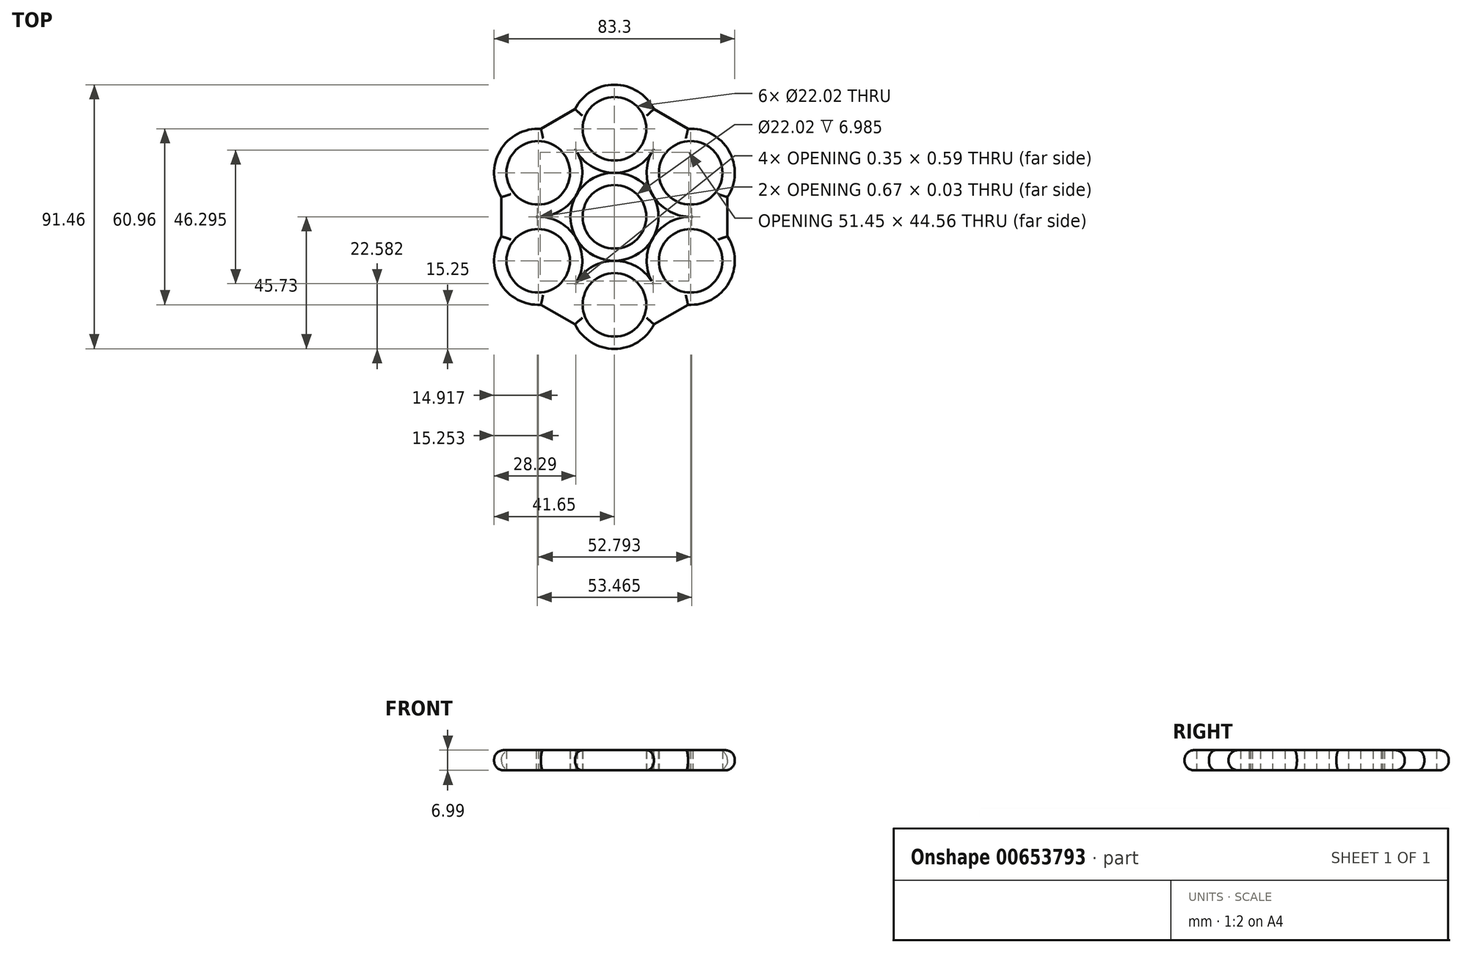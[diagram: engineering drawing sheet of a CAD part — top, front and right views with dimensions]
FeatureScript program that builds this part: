
annotation { "Feature Type Name" : "Feature", "Feature Type Description" : "" }
export const myFeature = defineFeature(function(context is Context, id is Id, definition is map)
    precondition{}
    {
        {
            var Q0;
            Q0=qCreatedBy(makeId("Top.planeOp"),FACE);
            var sketch = newSketch(context, id + "F0", { "sketchPlane" : qUnion([Q0])});
            skCircle(sketch, "E0", {"center": v(0, 0) * mm, "radius": 11.01 * mm});
            skLineSegment(sketch, "E1", {"start": v(0, 0) * mm, "end": v(0, 30.48) * mm});
            skLineSegment(sketch, "E2", {"start": v(0, 0) * mm, "end": v(26.4, -15.24) * mm});
            skLineSegment(sketch, "E3", {"start": v(0, 0) * mm, "end": v(-26.4, -15.24) * mm});
            skLineSegment(sketch, "E4", {"start": v(0, 0) * mm, "end": v(-26.4, 15.24) * mm});
            skLineSegment(sketch, "E5", {"start": v(0, 0) * mm, "end": v(0, -30.48) * mm});
            skLineSegment(sketch, "E6", {"start": v(0, 0) * mm, "end": v(26.4, 15.24) * mm});
            skCircle(sketch, "E7.cCircle", {"center": v(0, 30.48) * mm, "radius": 11.01 * mm, "construction": true});
            skLineSegment(sketch, "E7.0", {"start": v(6.36, 19.47) * mm, "end": v(-6.36, 19.47) * mm});
            skLineSegment(sketch, "E7.1", {"start": v(-6.36, 19.47) * mm, "end": v(-12.71, 30.48) * mm});
            skLineSegment(sketch, "E7.2", {"start": v(-12.71, 30.48) * mm, "end": v(-6.36, 41.5) * mm});
            skLineSegment(sketch, "E7.3", {"start": v(-6.36, 41.5) * mm, "end": v(6.36, 41.5) * mm});
            skLineSegment(sketch, "E7.4", {"start": v(6.36, 41.5) * mm, "end": v(12.71, 30.48) * mm});
            skLineSegment(sketch, "E7.5", {"start": v(12.71, 30.48) * mm, "end": v(6.36, 19.47) * mm});
            skPoint(sketch, "E7.0.midPoint", {"position": v(0, 19.47) * mm});
            skCircle(sketch, "E8.cCircle", {"center": v(26.4, 15.24) * mm, "radius": 11.01 * mm, "construction": true});
            skLineSegment(sketch, "E8.0", {"start": v(20.04, 4.23) * mm, "end": v(13.68, 15.24) * mm});
            skLineSegment(sketch, "E8.1", {"start": v(13.68, 15.24) * mm, "end": v(20.04, 26.25) * mm});
            skLineSegment(sketch, "E8.2", {"start": v(20.04, 26.25) * mm, "end": v(32.75, 26.25) * mm});
            skLineSegment(sketch, "E8.3", {"start": v(32.75, 26.25) * mm, "end": v(39.11, 15.24) * mm});
            skLineSegment(sketch, "E8.4", {"start": v(39.11, 15.24) * mm, "end": v(32.75, 4.23) * mm});
            skLineSegment(sketch, "E8.5", {"start": v(32.75, 4.23) * mm, "end": v(20.04, 4.23) * mm});
            skPoint(sketch, "E8.0.midPoint", {"position": v(16.86, 9.73) * mm});
            skCircle(sketch, "E9.cCircle", {"center": v(26.4, -15.24) * mm, "radius": 11.01 * mm, "construction": true});
            skLineSegment(sketch, "E9.0", {"start": v(13.68, -15.24) * mm, "end": v(20.04, -4.23) * mm});
            skLineSegment(sketch, "E9.1", {"start": v(20.04, -4.23) * mm, "end": v(32.75, -4.23) * mm});
            skLineSegment(sketch, "E9.2", {"start": v(32.75, -4.23) * mm, "end": v(39.11, -15.24) * mm});
            skLineSegment(sketch, "E9.3", {"start": v(39.11, -15.24) * mm, "end": v(32.75, -26.25) * mm});
            skLineSegment(sketch, "E9.4", {"start": v(32.75, -26.25) * mm, "end": v(20.04, -26.25) * mm});
            skLineSegment(sketch, "E9.5", {"start": v(20.04, -26.25) * mm, "end": v(13.68, -15.24) * mm});
            skPoint(sketch, "E9.0.midPoint", {"position": v(16.86, -9.73) * mm});
            skCircle(sketch, "E10.cCircle", {"center": v(0, -30.48) * mm, "radius": 11.01 * mm, "construction": true});
            skLineSegment(sketch, "E10.0", {"start": v(-6.36, -19.47) * mm, "end": v(6.36, -19.47) * mm});
            skLineSegment(sketch, "E10.1", {"start": v(6.36, -19.47) * mm, "end": v(12.71, -30.48) * mm});
            skLineSegment(sketch, "E10.2", {"start": v(12.71, -30.48) * mm, "end": v(6.36, -41.5) * mm});
            skLineSegment(sketch, "E10.3", {"start": v(6.36, -41.5) * mm, "end": v(-6.36, -41.5) * mm});
            skLineSegment(sketch, "E10.4", {"start": v(-6.36, -41.5) * mm, "end": v(-12.71, -30.48) * mm});
            skLineSegment(sketch, "E10.5", {"start": v(-12.71, -30.48) * mm, "end": v(-6.36, -19.47) * mm});
            skPoint(sketch, "E10.0.midPoint", {"position": v(0, -19.47) * mm});
            skCircle(sketch, "E11.cCircle", {"center": v(-26.4, -15.24) * mm, "radius": 11.01 * mm, "construction": true});
            skLineSegment(sketch, "E11.0", {"start": v(-20.04, -4.23) * mm, "end": v(-13.68, -15.24) * mm});
            skLineSegment(sketch, "E11.1", {"start": v(-13.68, -15.24) * mm, "end": v(-20.04, -26.25) * mm});
            skLineSegment(sketch, "E11.2", {"start": v(-20.04, -26.25) * mm, "end": v(-32.75, -26.25) * mm});
            skLineSegment(sketch, "E11.3", {"start": v(-32.75, -26.25) * mm, "end": v(-39.11, -15.24) * mm});
            skLineSegment(sketch, "E11.4", {"start": v(-39.11, -15.24) * mm, "end": v(-32.75, -4.23) * mm});
            skLineSegment(sketch, "E11.5", {"start": v(-32.75, -4.23) * mm, "end": v(-20.04, -4.23) * mm});
            skPoint(sketch, "E11.0.midPoint", {"position": v(-16.86, -9.73) * mm});
            skCircle(sketch, "E12.cCircle", {"center": v(-26.4, 15.24) * mm, "radius": 11.01 * mm, "construction": true});
            skLineSegment(sketch, "E12.0", {"start": v(-13.68, 15.24) * mm, "end": v(-20.04, 4.23) * mm});
            skLineSegment(sketch, "E12.1", {"start": v(-20.04, 4.23) * mm, "end": v(-32.75, 4.23) * mm});
            skLineSegment(sketch, "E12.2", {"start": v(-32.75, 4.23) * mm, "end": v(-39.11, 15.24) * mm});
            skLineSegment(sketch, "E12.3", {"start": v(-39.11, 15.24) * mm, "end": v(-32.75, 26.25) * mm});
            skLineSegment(sketch, "E12.4", {"start": v(-32.75, 26.25) * mm, "end": v(-20.04, 26.25) * mm});
            skLineSegment(sketch, "E12.5", {"start": v(-20.04, 26.25) * mm, "end": v(-13.68, 15.24) * mm});
            skPoint(sketch, "E12.0.midPoint", {"position": v(-16.86, 9.73) * mm});
            skCircle(sketch, "E13", {"center": v(0, 0) * mm, "radius": 15.23 * mm});
            skPoint(sketch, "E14.startSnap0", {"position": v(-16.86, 20.75) * mm});
            skLineSegment(sketch, "E15", {"start": v(-16.86, 20.75) * mm, "end": v(-9.54, 24.97) * mm});
            skLineSegment(sketch, "E16", {"start": v(-26.4, 4.23) * mm, "end": v(-26.4, -4.23) * mm});
            skLineSegment(sketch, "E17", {"start": v(26.4, 4.23) * mm, "end": v(26.4, -4.23) * mm});
            skLineSegment(sketch, "E18", {"start": v(-16.86, -20.75) * mm, "end": v(-9.54, -24.97) * mm});
            skLineSegment(sketch, "E19", {"start": v(16.86, -20.75) * mm, "end": v(9.54, -24.97) * mm});
            skLineSegment(sketch, "E20", {"start": v(16.86, 20.75) * mm, "end": v(9.54, 24.97) * mm});
            skLineSegment(sketch, "E21", {"start": v(-32.75, 26.25) * mm, "end": v(-6.36, 41.5) * mm});
            skLineSegment(sketch, "E22", {"start": v(-39.11, 15.24) * mm, "end": v(-39.11, -15.24) * mm});
            skLineSegment(sketch, "E23", {"start": v(39.11, 15.24) * mm, "end": v(39.11, -15.24) * mm});
            skLineSegment(sketch, "E24", {"start": v(6.36, -41.5) * mm, "end": v(32.75, -26.25) * mm});
            skLineSegment(sketch, "E25", {"start": v(-6.36, -41.5) * mm, "end": v(-32.75, -26.25) * mm});
            skLineSegment(sketch, "E26", {"start": v(6.36, 41.5) * mm, "end": v(32.75, 26.25) * mm});
            skCircle(sketch, "E27", {"center": v(-26.4, 15.24) * mm, "radius": 15.25 * mm});
            skCircle(sketch, "E28", {"center": v(0, 30.48) * mm, "radius": 15.25 * mm});
            skCircle(sketch, "E29", {"center": v(26.4, 15.24) * mm, "radius": 15.25 * mm});
            skCircle(sketch, "E30", {"center": v(26.4, -15.24) * mm, "radius": 15.25 * mm});
            skCircle(sketch, "E31", {"center": v(0, -30.48) * mm, "radius": 15.25 * mm});
            skCircle(sketch, "E32", {"center": v(-26.4, -15.24) * mm, "radius": 15.25 * mm});
            skCircle(sketch, "E33", {"center": v(0, 30.48) * mm, "radius": 11.01 * mm});
            skCircle(sketch, "E34", {"center": v(26.4, 15.24) * mm, "radius": 11.01 * mm});
            skCircle(sketch, "E35", {"center": v(26.4, -15.24) * mm, "radius": 11.01 * mm});
            skCircle(sketch, "E36", {"center": v(0, -30.48) * mm, "radius": 11.01 * mm});
            skCircle(sketch, "E37", {"center": v(-26.4, 15.24) * mm, "radius": 11.01 * mm});
            skCircle(sketch, "E38", {"center": v(-26.4, -15.24) * mm, "radius": 11.01 * mm});
            skSolve(sketch);
        }
        {
            var Q0;
            {var subQ3=sQuery(id+"F0.wireOp",EDGE,"E7.2");Q0=makeQuery(id+"F0.imprint","IMPRINT",FACE,{"disambiguationData":[TD([[makeQuery(id+"F0.imprint","IMPRINT",EDGE,{"derivedFrom":subQ3}),1.0]])]});}
            var Q1;
            {var subQ4=sQuery(id+"F0.wireOp",EDGE,"E7.4");Q1=makeQuery(id+"F0.imprint","IMPRINT",FACE,{"disambiguationData":[TD([[makeQuery(id+"F0.imprint","IMPRINT",EDGE,{"derivedFrom":subQ4}),1.0]])]});}
            var Q2;
            {var subQ4=sQuery(id+"F0.wireOp",EDGE,"E8.4");Q2=makeQuery(id+"F0.imprint","IMPRINT",FACE,{"disambiguationData":[TD([[makeQuery(id+"F0.imprint","IMPRINT",EDGE,{"derivedFrom":subQ4}),1.0]])]});}
            var Q3;
            {var subQ4=sQuery(id+"F0.wireOp",EDGE,"E9.4");Q3=makeQuery(id+"F0.imprint","IMPRINT",FACE,{"disambiguationData":[TD([[makeQuery(id+"F0.imprint","IMPRINT",EDGE,{"derivedFrom":subQ4}),1.0]])]});}
            var Q4;
            {var subQ4=sQuery(id+"F0.wireOp",EDGE,"E10.4");Q4=makeQuery(id+"F0.imprint","IMPRINT",FACE,{"disambiguationData":[TD([[makeQuery(id+"F0.imprint","IMPRINT",EDGE,{"derivedFrom":subQ4}),1.0]])]});}
            var Q5;
            {var subQ4=sQuery(id+"F0.wireOp",EDGE,"E11.4");Q5=makeQuery(id+"F0.imprint","IMPRINT",FACE,{"disambiguationData":[TD([[makeQuery(id+"F0.imprint","IMPRINT",EDGE,{"derivedFrom":subQ4}),1.0]])]});}
            var Q6;
            {var subQ0=sQuery(id+"F0.wireOp",EDGE,"E4");var subQ1=sQuery(id+"F0.wireOp",EDGE,"E0");var subQ2=makeQuery(id+"F0.imprint","INTERSECT",VERTEX,{"derivedFrom":[subQ1,subQ0]});Q6=makeQuery(id+"F0.imprint","IMPRINT",FACE,{"disambiguationData":[TD([[makeQuery(id+"F0.imprint","IMPRINT",EDGE,{"disambiguationData":[TD([[subQ2,-1.0]])],"derivedFrom":subQ1}),-1.0]])]});}
            var Q7;
            {var subQ0=sQuery(id+"F0.wireOp",EDGE,"E1");var subQ1=sQuery(id+"F0.wireOp",EDGE,"E0");var subQ2=makeQuery(id+"F0.imprint","INTERSECT",VERTEX,{"derivedFrom":[subQ1,subQ0]});Q7=makeQuery(id+"F0.imprint","IMPRINT",FACE,{"disambiguationData":[TD([[makeQuery(id+"F0.imprint","IMPRINT",EDGE,{"disambiguationData":[TD([[subQ2,-1.0]])],"derivedFrom":subQ1}),-1.0]])]});}
            var Q8;
            {var subQ0=sQuery(id+"F0.wireOp",EDGE,"E1");var subQ1=sQuery(id+"F0.wireOp",EDGE,"E0");var subQ2=makeQuery(id+"F0.imprint","INTERSECT",VERTEX,{"derivedFrom":[subQ1,subQ0]});Q8=makeQuery(id+"F0.imprint","IMPRINT",FACE,{"disambiguationData":[TD([[makeQuery(id+"F0.imprint","IMPRINT",EDGE,{"disambiguationData":[TD([[subQ2,1.0]])],"derivedFrom":subQ1}),-1.0]])]});}
            var Q9;
            {var subQ0=sQuery(id+"F0.wireOp",EDGE,"E6");var subQ1=sQuery(id+"F0.wireOp",EDGE,"E0");var subQ2=makeQuery(id+"F0.imprint","INTERSECT",VERTEX,{"derivedFrom":[subQ1,subQ0]});Q9=makeQuery(id+"F0.imprint","IMPRINT",FACE,{"disambiguationData":[TD([[makeQuery(id+"F0.imprint","IMPRINT",EDGE,{"disambiguationData":[TD([[subQ2,1.0]])],"derivedFrom":subQ1}),-1.0]])]});}
            var Q10;
            {var subQ0=sQuery(id+"F0.wireOp",EDGE,"E5");var subQ1=sQuery(id+"F0.wireOp",EDGE,"E0");var subQ2=makeQuery(id+"F0.imprint","INTERSECT",VERTEX,{"derivedFrom":[subQ1,subQ0]});Q10=makeQuery(id+"F0.imprint","IMPRINT",FACE,{"disambiguationData":[TD([[makeQuery(id+"F0.imprint","IMPRINT",EDGE,{"disambiguationData":[TD([[subQ2,-1.0]])],"derivedFrom":subQ1}),-1.0]])]});}
            var Q11;
            {var subQ0=sQuery(id+"F0.wireOp",EDGE,"E3");var subQ1=sQuery(id+"F0.wireOp",EDGE,"E0");var subQ2=makeQuery(id+"F0.imprint","INTERSECT",VERTEX,{"derivedFrom":[subQ1,subQ0]});Q11=makeQuery(id+"F0.imprint","IMPRINT",FACE,{"disambiguationData":[TD([[makeQuery(id+"F0.imprint","IMPRINT",EDGE,{"disambiguationData":[TD([[subQ2,-1.0]])],"derivedFrom":subQ1}),-1.0]])]});}
            var Q12;
            {var subQ8=sQuery(id+"F0.wireOp",EDGE,"E18");Q12=makeQuery(id+"F0.imprint","IMPRINT",FACE,{"disambiguationData":[TD([[makeQuery(id+"F0.imprint","IMPRINT",EDGE,{"derivedFrom":subQ8}),1.0]])]});}
            var Q13;
            {var subQ3=sQuery(id+"F0.wireOp",EDGE,"E16");Q13=makeQuery(id+"F0.imprint","IMPRINT",FACE,{"disambiguationData":[TD([[makeQuery(id+"F0.imprint","IMPRINT",EDGE,{"derivedFrom":subQ3}),1.0]])]});}
            var Q14;
            {var subQ3=sQuery(id+"F0.wireOp",EDGE,"E15");Q14=makeQuery(id+"F0.imprint","IMPRINT",FACE,{"disambiguationData":[TD([[makeQuery(id+"F0.imprint","IMPRINT",EDGE,{"derivedFrom":subQ3}),-1.0]])]});}
            var Q15;
            {var subQ3=sQuery(id+"F0.wireOp",EDGE,"E20");Q15=makeQuery(id+"F0.imprint","IMPRINT",FACE,{"disambiguationData":[TD([[makeQuery(id+"F0.imprint","IMPRINT",EDGE,{"derivedFrom":subQ3}),1.0]])]});}
            var Q16;
            {var subQ12=sQuery(id+"F0.wireOp",EDGE,"E17");Q16=makeQuery(id+"F0.imprint","IMPRINT",FACE,{"disambiguationData":[TD([[makeQuery(id+"F0.imprint","IMPRINT",EDGE,{"derivedFrom":subQ12}),-1.0]])]});}
            var Q17;
            {var subQ12=sQuery(id+"F0.wireOp",EDGE,"E19");Q17=makeQuery(id+"F0.imprint","IMPRINT",FACE,{"disambiguationData":[TD([[makeQuery(id+"F0.imprint","IMPRINT",EDGE,{"derivedFrom":subQ12}),-1.0]])]});}
            var Q18;
            {var subQ0=sQuery(id+"F0.wireOp",EDGE,"E10.3");Q18=makeQuery(id+"F0.imprint","IMPRINT",FACE,{"disambiguationData":[TD([[makeQuery(id+"F0.imprint","IMPRINT",EDGE,{"derivedFrom":subQ0}),1.0]])]});}
            var Q19;
            {var subQ1=sQuery(id+"F0.wireOp",EDGE,"E10.2");Q19=makeQuery(id+"F0.imprint","IMPRINT",FACE,{"disambiguationData":[TD([[makeQuery(id+"F0.imprint","IMPRINT",EDGE,{"derivedFrom":subQ1}),1.0]])]});}
            var Q20;
            {var subQ1=sQuery(id+"F0.wireOp",EDGE,"E10.1");var subQ5=sQuery(id+"F0.wireOp",EDGE,"E10.0");var subQ6=makeQuery(id+"F0.imprint","INTERSECT",VERTEX,{"derivedFrom":[subQ5,subQ1]});Q20=makeQuery(id+"F0.imprint","IMPRINT",FACE,{"disambiguationData":[TD([[makeQuery(id+"F0.imprint","IMPRINT",EDGE,{"disambiguationData":[TD([[subQ6,1.0]])],"derivedFrom":subQ5}),1.0]])]});}
            var Q21;
            {var subQ0=sQuery(id+"F0.wireOp",EDGE,"E10.5");var subQ1=sQuery(id+"F0.wireOp",EDGE,"E10.0");var subQ2=makeQuery(id+"F0.imprint","INTERSECT",VERTEX,{"derivedFrom":[subQ1,subQ0]});Q21=makeQuery(id+"F0.imprint","IMPRINT",FACE,{"disambiguationData":[TD([[makeQuery(id+"F0.imprint","IMPRINT",EDGE,{"disambiguationData":[TD([[subQ2,-1.0]])],"derivedFrom":subQ1}),1.0]])]});}
            var Q22;
            {var subQ1=sQuery(id+"F0.wireOp",EDGE,"E11.1");var subQ5=sQuery(id+"F0.wireOp",EDGE,"E11.0");var subQ6=makeQuery(id+"F0.imprint","INTERSECT",VERTEX,{"derivedFrom":[subQ5,subQ1]});Q22=makeQuery(id+"F0.imprint","IMPRINT",FACE,{"disambiguationData":[TD([[makeQuery(id+"F0.imprint","IMPRINT",EDGE,{"disambiguationData":[TD([[subQ6,1.0]])],"derivedFrom":subQ5}),1.0]])]});}
            var Q23;
            {var subQ1=sQuery(id+"F0.wireOp",EDGE,"E11.2");Q23=makeQuery(id+"F0.imprint","IMPRINT",FACE,{"disambiguationData":[TD([[makeQuery(id+"F0.imprint","IMPRINT",EDGE,{"derivedFrom":subQ1}),1.0]])]});}
            var Q24;
            {var subQ0=sQuery(id+"F0.wireOp",EDGE,"E11.3");Q24=makeQuery(id+"F0.imprint","IMPRINT",FACE,{"disambiguationData":[TD([[makeQuery(id+"F0.imprint","IMPRINT",EDGE,{"derivedFrom":subQ0}),1.0]])]});}
            var Q25;
            {var subQ0=sQuery(id+"F0.wireOp",EDGE,"E11.5");var subQ1=sQuery(id+"F0.wireOp",EDGE,"E11.0");var subQ2=makeQuery(id+"F0.imprint","INTERSECT",VERTEX,{"derivedFrom":[subQ1,subQ0]});Q25=makeQuery(id+"F0.imprint","IMPRINT",FACE,{"disambiguationData":[TD([[makeQuery(id+"F0.imprint","IMPRINT",EDGE,{"disambiguationData":[TD([[subQ2,-1.0]])],"derivedFrom":subQ1}),1.0]])]});}
            var Q26;
            {var subQ0=sQuery(id+"F0.wireOp",EDGE,"E12.1");var subQ1=sQuery(id+"F0.wireOp",EDGE,"E12.0");var subQ2=makeQuery(id+"F0.imprint","INTERSECT",VERTEX,{"derivedFrom":[subQ1,subQ0]});Q26=makeQuery(id+"F0.imprint","IMPRINT",FACE,{"disambiguationData":[TD([[makeQuery(id+"F0.imprint","IMPRINT",EDGE,{"disambiguationData":[TD([[subQ2,1.0]])],"derivedFrom":subQ1}),1.0]])]});}
            var Q27;
            {var subQ1=sQuery(id+"F0.wireOp",EDGE,"E12.2");Q27=makeQuery(id+"F0.imprint","IMPRINT",FACE,{"disambiguationData":[TD([[makeQuery(id+"F0.imprint","IMPRINT",EDGE,{"derivedFrom":subQ1}),1.0]])]});}
            var Q28;
            {var subQ0=sQuery(id+"F0.wireOp",EDGE,"E12.3");Q28=makeQuery(id+"F0.imprint","IMPRINT",FACE,{"disambiguationData":[TD([[makeQuery(id+"F0.imprint","IMPRINT",EDGE,{"derivedFrom":subQ0}),1.0]])]});}
            var Q29;
            {var subQ1=sQuery(id+"F0.wireOp",EDGE,"E12.4");Q29=makeQuery(id+"F0.imprint","IMPRINT",FACE,{"disambiguationData":[TD([[makeQuery(id+"F0.imprint","IMPRINT",EDGE,{"derivedFrom":subQ1}),1.0]])]});}
            var Q30;
            {var subQ1=sQuery(id+"F0.wireOp",EDGE,"E12.5");var subQ9=sQuery(id+"F0.wireOp",EDGE,"E12.0");var subQ10=makeQuery(id+"F0.imprint","INTERSECT",VERTEX,{"derivedFrom":[subQ9,subQ1]});Q30=makeQuery(id+"F0.imprint","IMPRINT",FACE,{"disambiguationData":[TD([[makeQuery(id+"F0.imprint","IMPRINT",EDGE,{"disambiguationData":[TD([[subQ10,-1.0]])],"derivedFrom":subQ9}),1.0]])]});}
            var Q31;
            {var subQ1=sQuery(id+"F0.wireOp",EDGE,"E7.1");var subQ5=sQuery(id+"F0.wireOp",EDGE,"E7.0");var subQ6=makeQuery(id+"F0.imprint","INTERSECT",VERTEX,{"derivedFrom":[subQ5,subQ1]});Q31=makeQuery(id+"F0.imprint","IMPRINT",FACE,{"disambiguationData":[TD([[makeQuery(id+"F0.imprint","IMPRINT",EDGE,{"disambiguationData":[TD([[subQ6,1.0]])],"derivedFrom":subQ5}),1.0]])]});}
            var Q32;
            {var subQ1=sQuery(id+"F0.wireOp",EDGE,"E7.5");var subQ5=sQuery(id+"F0.wireOp",EDGE,"E7.0");var subQ6=makeQuery(id+"F0.imprint","INTERSECT",VERTEX,{"derivedFrom":[subQ5,subQ1]});Q32=makeQuery(id+"F0.imprint","IMPRINT",FACE,{"disambiguationData":[TD([[makeQuery(id+"F0.imprint","IMPRINT",EDGE,{"disambiguationData":[TD([[subQ6,-1.0]])],"derivedFrom":subQ5}),1.0]])]});}
            var Q33;
            {var subQ0=sQuery(id+"F0.wireOp",EDGE,"E7.3");Q33=makeQuery(id+"F0.imprint","IMPRINT",FACE,{"disambiguationData":[TD([[makeQuery(id+"F0.imprint","IMPRINT",EDGE,{"derivedFrom":subQ0}),1.0]])]});}
            var Q34;
            {var subQ1=sQuery(id+"F0.wireOp",EDGE,"E8.2");Q34=makeQuery(id+"F0.imprint","IMPRINT",FACE,{"disambiguationData":[TD([[makeQuery(id+"F0.imprint","IMPRINT",EDGE,{"derivedFrom":subQ1}),1.0]])]});}
            var Q35;
            {var subQ0=sQuery(id+"F0.wireOp",EDGE,"E8.3");Q35=makeQuery(id+"F0.imprint","IMPRINT",FACE,{"disambiguationData":[TD([[makeQuery(id+"F0.imprint","IMPRINT",EDGE,{"derivedFrom":subQ0}),1.0]])]});}
            var Q36;
            {var subQ1=sQuery(id+"F0.wireOp",EDGE,"E8.5");var subQ5=sQuery(id+"F0.wireOp",EDGE,"E8.0");var subQ6=makeQuery(id+"F0.imprint","INTERSECT",VERTEX,{"derivedFrom":[subQ5,subQ1]});Q36=makeQuery(id+"F0.imprint","IMPRINT",FACE,{"disambiguationData":[TD([[makeQuery(id+"F0.imprint","IMPRINT",EDGE,{"disambiguationData":[TD([[subQ6,-1.0]])],"derivedFrom":subQ5}),1.0]])]});}
            var Q37;
            {var subQ0=sQuery(id+"F0.wireOp",EDGE,"E8.1");var subQ1=sQuery(id+"F0.wireOp",EDGE,"E8.0");var subQ2=makeQuery(id+"F0.imprint","INTERSECT",VERTEX,{"derivedFrom":[subQ1,subQ0]});Q37=makeQuery(id+"F0.imprint","IMPRINT",FACE,{"disambiguationData":[TD([[makeQuery(id+"F0.imprint","IMPRINT",EDGE,{"disambiguationData":[TD([[subQ2,1.0]])],"derivedFrom":subQ1}),1.0]])]});}
            var Q38;
            {var subQ1=sQuery(id+"F0.wireOp",EDGE,"E9.1");var subQ5=sQuery(id+"F0.wireOp",EDGE,"E9.0");var subQ6=makeQuery(id+"F0.imprint","INTERSECT",VERTEX,{"derivedFrom":[subQ5,subQ1]});Q38=makeQuery(id+"F0.imprint","IMPRINT",FACE,{"disambiguationData":[TD([[makeQuery(id+"F0.imprint","IMPRINT",EDGE,{"disambiguationData":[TD([[subQ6,1.0]])],"derivedFrom":subQ5}),1.0]])]});}
            var Q39;
            {var subQ0=sQuery(id+"F0.wireOp",EDGE,"E9.5");var subQ1=sQuery(id+"F0.wireOp",EDGE,"E9.0");var subQ2=makeQuery(id+"F0.imprint","INTERSECT",VERTEX,{"derivedFrom":[subQ1,subQ0]});Q39=makeQuery(id+"F0.imprint","IMPRINT",FACE,{"disambiguationData":[TD([[makeQuery(id+"F0.imprint","IMPRINT",EDGE,{"disambiguationData":[TD([[subQ2,-1.0]])],"derivedFrom":subQ1}),1.0]])]});}
            var Q40;
            {var subQ0=sQuery(id+"F0.wireOp",EDGE,"E9.3");Q40=makeQuery(id+"F0.imprint","IMPRINT",FACE,{"disambiguationData":[TD([[makeQuery(id+"F0.imprint","IMPRINT",EDGE,{"derivedFrom":subQ0}),1.0]])]});}
            var Q41;
            {var subQ9=sQuery(id+"F0.wireOp",EDGE,"E9.2");Q41=makeQuery(id+"F0.imprint","IMPRINT",FACE,{"disambiguationData":[TD([[makeQuery(id+"F0.imprint","IMPRINT",EDGE,{"derivedFrom":subQ9}),1.0]])]});}
            var Q42;
            {var subQ0=sQuery(id+"F0.wireOp",EDGE,"E27");var subQ1=sQuery(id+"F0.wireOp",EDGE,"E21");var subQ2=makeQuery(id+"F0.imprint","INTERSECT",VERTEX,{"derivedFrom":[subQ1,subQ0]});Q42=makeQuery(id+"F0.imprint","IMPRINT",FACE,{"disambiguationData":[TD([[makeQuery(id+"F0.imprint","IMPRINT",EDGE,{"disambiguationData":[TD([[subQ2,-1.0]])],"derivedFrom":subQ1}),-1.0]])]});}
            var Q43;
            {var subQ0=sQuery(id+"F0.wireOp",EDGE,"E28");var subQ1=sQuery(id+"F0.wireOp",EDGE,"E26");var subQ2=makeQuery(id+"F0.imprint","INTERSECT",VERTEX,{"derivedFrom":[subQ1,subQ0]});Q43=makeQuery(id+"F0.imprint","IMPRINT",FACE,{"disambiguationData":[TD([[makeQuery(id+"F0.imprint","IMPRINT",EDGE,{"disambiguationData":[TD([[subQ2,-1.0]])],"derivedFrom":subQ1}),-1.0]])]});}
            var Q44;
            {var subQ0=sQuery(id+"F0.wireOp",EDGE,"E29");var subQ1=sQuery(id+"F0.wireOp",EDGE,"E23");var subQ2=makeQuery(id+"F0.imprint","INTERSECT",VERTEX,{"derivedFrom":[subQ1,subQ0]});Q44=makeQuery(id+"F0.imprint","IMPRINT",FACE,{"disambiguationData":[TD([[makeQuery(id+"F0.imprint","IMPRINT",EDGE,{"disambiguationData":[TD([[subQ2,-1.0]])],"derivedFrom":subQ1}),-1.0]])]});}
            var Q45;
            {var subQ0=sQuery(id+"F0.wireOp",EDGE,"E31");var subQ1=sQuery(id+"F0.wireOp",EDGE,"E24");var subQ2=makeQuery(id+"F0.imprint","INTERSECT",VERTEX,{"derivedFrom":[subQ1,subQ0]});Q45=makeQuery(id+"F0.imprint","IMPRINT",FACE,{"disambiguationData":[TD([[makeQuery(id+"F0.imprint","IMPRINT",EDGE,{"disambiguationData":[TD([[subQ2,-1.0]])],"derivedFrom":subQ1}),1.0]])]});}
            var Q46;
            {var subQ0=sQuery(id+"F0.wireOp",EDGE,"E31");var subQ1=sQuery(id+"F0.wireOp",EDGE,"E25");var subQ2=makeQuery(id+"F0.imprint","INTERSECT",VERTEX,{"derivedFrom":[subQ1,subQ0]});Q46=makeQuery(id+"F0.imprint","IMPRINT",FACE,{"disambiguationData":[TD([[makeQuery(id+"F0.imprint","IMPRINT",EDGE,{"disambiguationData":[TD([[subQ2,-1.0]])],"derivedFrom":subQ1}),-1.0]])]});}
            var Q47;
            {var subQ0=sQuery(id+"F0.wireOp",EDGE,"E27");var subQ1=sQuery(id+"F0.wireOp",EDGE,"E22");var subQ2=makeQuery(id+"F0.imprint","INTERSECT",VERTEX,{"derivedFrom":[subQ1,subQ0]});Q47=makeQuery(id+"F0.imprint","IMPRINT",FACE,{"disambiguationData":[TD([[makeQuery(id+"F0.imprint","IMPRINT",EDGE,{"disambiguationData":[TD([[subQ2,-1.0]])],"derivedFrom":subQ1}),1.0]])]});}
            var Q48;
            {var subQ1=sQuery(id+"F0.wireOp",EDGE,"E12.2");var subQ3=sQuery(id+"F0.wireOp",EDGE,"E37");var subQ4=makeQuery(id+"F0.imprint","INTERSECT",VERTEX,{"derivedFrom":[subQ1,subQ3]});Q48=makeQuery(id+"F0.imprint","IMPRINT",FACE,{"disambiguationData":[TD([[makeQuery(id+"F0.imprint","IMPRINT",EDGE,{"disambiguationData":[TD([[subQ4,1.0]])],"derivedFrom":subQ3}),-1.0]])]});}
            var Q49;
            {var subQ1=sQuery(id+"F0.wireOp",EDGE,"E12.3");var subQ3=sQuery(id+"F0.wireOp",EDGE,"E37");var subQ4=makeQuery(id+"F0.imprint","INTERSECT",VERTEX,{"derivedFrom":[subQ1,subQ3]});Q49=makeQuery(id+"F0.imprint","IMPRINT",FACE,{"disambiguationData":[TD([[makeQuery(id+"F0.imprint","IMPRINT",EDGE,{"disambiguationData":[TD([[subQ4,1.0]])],"derivedFrom":subQ3}),-1.0]])]});}
            var Q50;
            {var subQ0=sQuery(id+"F0.wireOp",EDGE,"E12.5");var subQ1=sQuery(id+"F0.wireOp",EDGE,"E12.4");var subQ2=makeQuery(id+"F0.imprint","INTERSECT",VERTEX,{"derivedFrom":[subQ1,subQ0]});Q50=makeQuery(id+"F0.imprint","IMPRINT",FACE,{"disambiguationData":[TD([[makeQuery(id+"F0.imprint","IMPRINT",EDGE,{"disambiguationData":[TD([[subQ2,1.0]])],"derivedFrom":subQ1}),-1.0]])]});}
            var Q51;
            {var subQ0=sQuery(id+"F0.wireOp",EDGE,"E12.5");var subQ1=sQuery(id+"F0.wireOp",EDGE,"E12.0");var subQ2=makeQuery(id+"F0.imprint","INTERSECT",VERTEX,{"derivedFrom":[subQ1,subQ0]});Q51=makeQuery(id+"F0.imprint","IMPRINT",FACE,{"disambiguationData":[TD([[makeQuery(id+"F0.imprint","IMPRINT",EDGE,{"disambiguationData":[TD([[subQ2,-1.0]])],"derivedFrom":subQ1}),-1.0]])]});}
            var Q52;
            {var subQ0=sQuery(id+"F0.wireOp",EDGE,"E12.1");var subQ1=sQuery(id+"F0.wireOp",EDGE,"E12.0");var subQ2=makeQuery(id+"F0.imprint","INTERSECT",VERTEX,{"derivedFrom":[subQ1,subQ0]});Q52=makeQuery(id+"F0.imprint","IMPRINT",FACE,{"disambiguationData":[TD([[makeQuery(id+"F0.imprint","IMPRINT",EDGE,{"disambiguationData":[TD([[subQ2,1.0]])],"derivedFrom":subQ1}),-1.0]])]});}
            var Q53;
            {var subQ0=sQuery(id+"F0.wireOp",EDGE,"E12.2");var subQ1=sQuery(id+"F0.wireOp",EDGE,"E12.1");var subQ2=makeQuery(id+"F0.imprint","INTERSECT",VERTEX,{"derivedFrom":[subQ1,subQ0]});Q53=makeQuery(id+"F0.imprint","IMPRINT",FACE,{"disambiguationData":[TD([[makeQuery(id+"F0.imprint","IMPRINT",EDGE,{"disambiguationData":[TD([[subQ2,-1.0]])],"derivedFrom":subQ0}),-1.0]])]});}
            var Q54;
            {var subQ0=sQuery(id+"F0.wireOp",EDGE,"E11.5");var subQ1=sQuery(id+"F0.wireOp",EDGE,"E11.4");var subQ2=makeQuery(id+"F0.imprint","INTERSECT",VERTEX,{"derivedFrom":[subQ1,subQ0]});Q54=makeQuery(id+"F0.imprint","IMPRINT",FACE,{"disambiguationData":[TD([[makeQuery(id+"F0.imprint","IMPRINT",EDGE,{"disambiguationData":[TD([[subQ2,1.0]])],"derivedFrom":subQ1}),-1.0]])]});}
            var Q55;
            {var subQ1=sQuery(id+"F0.wireOp",EDGE,"E11.3");var subQ3=sQuery(id+"F0.wireOp",EDGE,"E38");var subQ4=makeQuery(id+"F0.imprint","INTERSECT",VERTEX,{"derivedFrom":[subQ1,subQ3]});Q55=makeQuery(id+"F0.imprint","IMPRINT",FACE,{"disambiguationData":[TD([[makeQuery(id+"F0.imprint","IMPRINT",EDGE,{"disambiguationData":[TD([[subQ4,1.0]])],"derivedFrom":subQ3}),-1.0]])]});}
            var Q56;
            {var subQ1=sQuery(id+"F0.wireOp",EDGE,"E11.2");var subQ3=sQuery(id+"F0.wireOp",EDGE,"E38");var subQ4=makeQuery(id+"F0.imprint","INTERSECT",VERTEX,{"derivedFrom":[subQ1,subQ3]});Q56=makeQuery(id+"F0.imprint","IMPRINT",FACE,{"disambiguationData":[TD([[makeQuery(id+"F0.imprint","IMPRINT",EDGE,{"disambiguationData":[TD([[subQ4,1.0]])],"derivedFrom":subQ3}),-1.0]])]});}
            var Q57;
            {var subQ0=sQuery(id+"F0.wireOp",EDGE,"E11.2");var subQ1=sQuery(id+"F0.wireOp",EDGE,"E11.1");var subQ2=makeQuery(id+"F0.imprint","INTERSECT",VERTEX,{"derivedFrom":[subQ1,subQ0]});Q57=makeQuery(id+"F0.imprint","IMPRINT",FACE,{"disambiguationData":[TD([[makeQuery(id+"F0.imprint","IMPRINT",EDGE,{"disambiguationData":[TD([[subQ2,-1.0]])],"derivedFrom":subQ0}),-1.0]])]});}
            var Q58;
            {var subQ0=sQuery(id+"F0.wireOp",EDGE,"E11.1");var subQ1=sQuery(id+"F0.wireOp",EDGE,"E11.0");var subQ2=makeQuery(id+"F0.imprint","INTERSECT",VERTEX,{"derivedFrom":[subQ1,subQ0]});Q58=makeQuery(id+"F0.imprint","IMPRINT",FACE,{"disambiguationData":[TD([[makeQuery(id+"F0.imprint","IMPRINT",EDGE,{"disambiguationData":[TD([[subQ2,1.0]])],"derivedFrom":subQ1}),-1.0]])]});}
            var Q59;
            {var subQ0=sQuery(id+"F0.wireOp",EDGE,"E11.5");var subQ1=sQuery(id+"F0.wireOp",EDGE,"E11.0");var subQ2=makeQuery(id+"F0.imprint","INTERSECT",VERTEX,{"derivedFrom":[subQ1,subQ0]});Q59=makeQuery(id+"F0.imprint","IMPRINT",FACE,{"disambiguationData":[TD([[makeQuery(id+"F0.imprint","IMPRINT",EDGE,{"disambiguationData":[TD([[subQ2,-1.0]])],"derivedFrom":subQ1}),-1.0]])]});}
            var Q60;
            {var subQ0=sQuery(id+"F0.wireOp",EDGE,"E10.5");var subQ1=sQuery(id+"F0.wireOp",EDGE,"E10.0");var subQ2=makeQuery(id+"F0.imprint","INTERSECT",VERTEX,{"derivedFrom":[subQ1,subQ0]});Q60=makeQuery(id+"F0.imprint","IMPRINT",FACE,{"disambiguationData":[TD([[makeQuery(id+"F0.imprint","IMPRINT",EDGE,{"disambiguationData":[TD([[subQ2,-1.0]])],"derivedFrom":subQ1}),-1.0]])]});}
            var Q61;
            {var subQ0=sQuery(id+"F0.wireOp",EDGE,"E10.1");var subQ1=sQuery(id+"F0.wireOp",EDGE,"E10.0");var subQ2=makeQuery(id+"F0.imprint","INTERSECT",VERTEX,{"derivedFrom":[subQ1,subQ0]});Q61=makeQuery(id+"F0.imprint","IMPRINT",FACE,{"disambiguationData":[TD([[makeQuery(id+"F0.imprint","IMPRINT",EDGE,{"disambiguationData":[TD([[subQ2,1.0]])],"derivedFrom":subQ1}),-1.0]])]});}
            var Q62;
            {var subQ0=sQuery(id+"F0.wireOp",EDGE,"E10.2");var subQ1=sQuery(id+"F0.wireOp",EDGE,"E10.1");var subQ2=makeQuery(id+"F0.imprint","INTERSECT",VERTEX,{"derivedFrom":[subQ1,subQ0]});Q62=makeQuery(id+"F0.imprint","IMPRINT",FACE,{"disambiguationData":[TD([[makeQuery(id+"F0.imprint","IMPRINT",EDGE,{"disambiguationData":[TD([[subQ2,-1.0]])],"derivedFrom":subQ0}),-1.0]])]});}
            var Q63;
            {var subQ1=sQuery(id+"F0.wireOp",EDGE,"E10.2");var subQ3=sQuery(id+"F0.wireOp",EDGE,"E36");var subQ4=makeQuery(id+"F0.imprint","INTERSECT",VERTEX,{"derivedFrom":[subQ1,subQ3]});Q63=makeQuery(id+"F0.imprint","IMPRINT",FACE,{"disambiguationData":[TD([[makeQuery(id+"F0.imprint","IMPRINT",EDGE,{"disambiguationData":[TD([[subQ4,1.0]])],"derivedFrom":subQ3}),-1.0]])]});}
            var Q64;
            {var subQ1=sQuery(id+"F0.wireOp",EDGE,"E10.3");var subQ3=sQuery(id+"F0.wireOp",EDGE,"E36");var subQ4=makeQuery(id+"F0.imprint","INTERSECT",VERTEX,{"derivedFrom":[subQ1,subQ3]});Q64=makeQuery(id+"F0.imprint","IMPRINT",FACE,{"disambiguationData":[TD([[makeQuery(id+"F0.imprint","IMPRINT",EDGE,{"disambiguationData":[TD([[subQ4,1.0]])],"derivedFrom":subQ3}),-1.0]])]});}
            var Q65;
            {var subQ0=sQuery(id+"F0.wireOp",EDGE,"E10.5");var subQ1=sQuery(id+"F0.wireOp",EDGE,"E10.4");var subQ2=makeQuery(id+"F0.imprint","INTERSECT",VERTEX,{"derivedFrom":[subQ1,subQ0]});Q65=makeQuery(id+"F0.imprint","IMPRINT",FACE,{"disambiguationData":[TD([[makeQuery(id+"F0.imprint","IMPRINT",EDGE,{"disambiguationData":[TD([[subQ2,1.0]])],"derivedFrom":subQ1}),-1.0]])]});}
            var Q66;
            {var subQ0=sQuery(id+"F0.wireOp",EDGE,"E9.2");var subQ1=sQuery(id+"F0.wireOp",EDGE,"E9.1");var subQ2=makeQuery(id+"F0.imprint","INTERSECT",VERTEX,{"derivedFrom":[subQ1,subQ0]});Q66=makeQuery(id+"F0.imprint","IMPRINT",FACE,{"disambiguationData":[TD([[makeQuery(id+"F0.imprint","IMPRINT",EDGE,{"disambiguationData":[TD([[subQ2,-1.0]])],"derivedFrom":subQ0}),-1.0]])]});}
            var Q67;
            {var subQ1=sQuery(id+"F0.wireOp",EDGE,"E9.2");var subQ3=sQuery(id+"F0.wireOp",EDGE,"E35");var subQ4=makeQuery(id+"F0.imprint","INTERSECT",VERTEX,{"derivedFrom":[subQ1,subQ3]});Q67=makeQuery(id+"F0.imprint","IMPRINT",FACE,{"disambiguationData":[TD([[makeQuery(id+"F0.imprint","IMPRINT",EDGE,{"disambiguationData":[TD([[subQ4,1.0]])],"derivedFrom":subQ3}),-1.0]])]});}
            var Q68;
            {var subQ1=sQuery(id+"F0.wireOp",EDGE,"E9.3");var subQ3=sQuery(id+"F0.wireOp",EDGE,"E35");var subQ4=makeQuery(id+"F0.imprint","INTERSECT",VERTEX,{"derivedFrom":[subQ1,subQ3]});Q68=makeQuery(id+"F0.imprint","IMPRINT",FACE,{"disambiguationData":[TD([[makeQuery(id+"F0.imprint","IMPRINT",EDGE,{"disambiguationData":[TD([[subQ4,1.0]])],"derivedFrom":subQ3}),-1.0]])]});}
            var Q69;
            {var subQ0=sQuery(id+"F0.wireOp",EDGE,"E9.5");var subQ1=sQuery(id+"F0.wireOp",EDGE,"E9.4");var subQ2=makeQuery(id+"F0.imprint","INTERSECT",VERTEX,{"derivedFrom":[subQ1,subQ0]});Q69=makeQuery(id+"F0.imprint","IMPRINT",FACE,{"disambiguationData":[TD([[makeQuery(id+"F0.imprint","IMPRINT",EDGE,{"disambiguationData":[TD([[subQ2,1.0]])],"derivedFrom":subQ1}),-1.0]])]});}
            var Q70;
            {var subQ0=sQuery(id+"F0.wireOp",EDGE,"E9.5");var subQ1=sQuery(id+"F0.wireOp",EDGE,"E9.0");var subQ2=makeQuery(id+"F0.imprint","INTERSECT",VERTEX,{"derivedFrom":[subQ1,subQ0]});Q70=makeQuery(id+"F0.imprint","IMPRINT",FACE,{"disambiguationData":[TD([[makeQuery(id+"F0.imprint","IMPRINT",EDGE,{"disambiguationData":[TD([[subQ2,-1.0]])],"derivedFrom":subQ1}),-1.0]])]});}
            var Q71;
            {var subQ0=sQuery(id+"F0.wireOp",EDGE,"E8.1");var subQ1=sQuery(id+"F0.wireOp",EDGE,"E8.0");var subQ2=makeQuery(id+"F0.imprint","INTERSECT",VERTEX,{"derivedFrom":[subQ1,subQ0]});Q71=makeQuery(id+"F0.imprint","IMPRINT",FACE,{"disambiguationData":[TD([[makeQuery(id+"F0.imprint","IMPRINT",EDGE,{"disambiguationData":[TD([[subQ2,1.0]])],"derivedFrom":subQ1}),-1.0]])]});}
            var Q72;
            {var subQ0=sQuery(id+"F0.wireOp",EDGE,"E8.2");var subQ1=sQuery(id+"F0.wireOp",EDGE,"E8.1");var subQ2=makeQuery(id+"F0.imprint","INTERSECT",VERTEX,{"derivedFrom":[subQ1,subQ0]});Q72=makeQuery(id+"F0.imprint","IMPRINT",FACE,{"disambiguationData":[TD([[makeQuery(id+"F0.imprint","IMPRINT",EDGE,{"disambiguationData":[TD([[subQ2,-1.0]])],"derivedFrom":subQ0}),-1.0]])]});}
            var Q73;
            {var subQ1=sQuery(id+"F0.wireOp",EDGE,"E8.2");var subQ3=sQuery(id+"F0.wireOp",EDGE,"E34");var subQ4=makeQuery(id+"F0.imprint","INTERSECT",VERTEX,{"derivedFrom":[subQ1,subQ3]});Q73=makeQuery(id+"F0.imprint","IMPRINT",FACE,{"disambiguationData":[TD([[makeQuery(id+"F0.imprint","IMPRINT",EDGE,{"disambiguationData":[TD([[subQ4,1.0]])],"derivedFrom":subQ3}),-1.0]])]});}
            var Q74;
            {var subQ1=sQuery(id+"F0.wireOp",EDGE,"E8.3");var subQ3=sQuery(id+"F0.wireOp",EDGE,"E34");var subQ4=makeQuery(id+"F0.imprint","INTERSECT",VERTEX,{"derivedFrom":[subQ1,subQ3]});Q74=makeQuery(id+"F0.imprint","IMPRINT",FACE,{"disambiguationData":[TD([[makeQuery(id+"F0.imprint","IMPRINT",EDGE,{"disambiguationData":[TD([[subQ4,1.0]])],"derivedFrom":subQ3}),-1.0]])]});}
            var Q75;
            {var subQ0=sQuery(id+"F0.wireOp",EDGE,"E8.5");var subQ1=sQuery(id+"F0.wireOp",EDGE,"E8.4");var subQ2=makeQuery(id+"F0.imprint","INTERSECT",VERTEX,{"derivedFrom":[subQ1,subQ0]});Q75=makeQuery(id+"F0.imprint","IMPRINT",FACE,{"disambiguationData":[TD([[makeQuery(id+"F0.imprint","IMPRINT",EDGE,{"disambiguationData":[TD([[subQ2,1.0]])],"derivedFrom":subQ1}),-1.0]])]});}
            var Q76;
            {var subQ0=sQuery(id+"F0.wireOp",EDGE,"E8.5");var subQ1=sQuery(id+"F0.wireOp",EDGE,"E8.0");var subQ2=makeQuery(id+"F0.imprint","INTERSECT",VERTEX,{"derivedFrom":[subQ1,subQ0]});Q76=makeQuery(id+"F0.imprint","IMPRINT",FACE,{"disambiguationData":[TD([[makeQuery(id+"F0.imprint","IMPRINT",EDGE,{"disambiguationData":[TD([[subQ2,-1.0]])],"derivedFrom":subQ1}),-1.0]])]});}
            var Q77;
            {var subQ1=sQuery(id+"F0.wireOp",EDGE,"E7.2");var subQ3=sQuery(id+"F0.wireOp",EDGE,"E33");var subQ4=makeQuery(id+"F0.imprint","INTERSECT",VERTEX,{"derivedFrom":[subQ1,subQ3]});Q77=makeQuery(id+"F0.imprint","IMPRINT",FACE,{"disambiguationData":[TD([[makeQuery(id+"F0.imprint","IMPRINT",EDGE,{"disambiguationData":[TD([[subQ4,1.0]])],"derivedFrom":subQ3}),-1.0]])]});}
            var Q78;
            {var subQ1=sQuery(id+"F0.wireOp",EDGE,"E7.3");var subQ3=sQuery(id+"F0.wireOp",EDGE,"E33");var subQ4=makeQuery(id+"F0.imprint","INTERSECT",VERTEX,{"derivedFrom":[subQ1,subQ3]});Q78=makeQuery(id+"F0.imprint","IMPRINT",FACE,{"disambiguationData":[TD([[makeQuery(id+"F0.imprint","IMPRINT",EDGE,{"disambiguationData":[TD([[subQ4,1.0]])],"derivedFrom":subQ3}),-1.0]])]});}
            var Q79;
            {var subQ0=sQuery(id+"F0.wireOp",EDGE,"E7.2");var subQ1=sQuery(id+"F0.wireOp",EDGE,"E7.1");var subQ2=makeQuery(id+"F0.imprint","INTERSECT",VERTEX,{"derivedFrom":[subQ1,subQ0]});Q79=makeQuery(id+"F0.imprint","IMPRINT",FACE,{"disambiguationData":[TD([[makeQuery(id+"F0.imprint","IMPRINT",EDGE,{"disambiguationData":[TD([[subQ2,-1.0]])],"derivedFrom":subQ0}),-1.0]])]});}
            var Q80;
            {var subQ0=sQuery(id+"F0.wireOp",EDGE,"E7.5");var subQ1=sQuery(id+"F0.wireOp",EDGE,"E7.4");var subQ2=makeQuery(id+"F0.imprint","INTERSECT",VERTEX,{"derivedFrom":[subQ1,subQ0]});Q80=makeQuery(id+"F0.imprint","IMPRINT",FACE,{"disambiguationData":[TD([[makeQuery(id+"F0.imprint","IMPRINT",EDGE,{"disambiguationData":[TD([[subQ2,1.0]])],"derivedFrom":subQ1}),-1.0]])]});}
            var Q81;
            {var subQ0=sQuery(id+"F0.wireOp",EDGE,"E7.5");var subQ1=sQuery(id+"F0.wireOp",EDGE,"E7.0");var subQ2=makeQuery(id+"F0.imprint","INTERSECT",VERTEX,{"derivedFrom":[subQ1,subQ0]});Q81=makeQuery(id+"F0.imprint","IMPRINT",FACE,{"disambiguationData":[TD([[makeQuery(id+"F0.imprint","IMPRINT",EDGE,{"disambiguationData":[TD([[subQ2,-1.0]])],"derivedFrom":subQ1}),-1.0]])]});}
            var Q82;
            {var subQ0=sQuery(id+"F0.wireOp",EDGE,"E7.1");var subQ1=sQuery(id+"F0.wireOp",EDGE,"E7.0");var subQ2=makeQuery(id+"F0.imprint","INTERSECT",VERTEX,{"derivedFrom":[subQ1,subQ0]});Q82=makeQuery(id+"F0.imprint","IMPRINT",FACE,{"disambiguationData":[TD([[makeQuery(id+"F0.imprint","IMPRINT",EDGE,{"disambiguationData":[TD([[subQ2,1.0]])],"derivedFrom":subQ1}),-1.0]])]});}
            var Q83;
            {var subQ0=sQuery(id+"F0.wireOp",EDGE,"E9.1");var subQ1=sQuery(id+"F0.wireOp",EDGE,"E9.0");var subQ2=makeQuery(id+"F0.imprint","INTERSECT",VERTEX,{"derivedFrom":[subQ1,subQ0]});Q83=makeQuery(id+"F0.imprint","IMPRINT",FACE,{"disambiguationData":[TD([[makeQuery(id+"F0.imprint","IMPRINT",EDGE,{"disambiguationData":[TD([[subQ2,1.0]])],"derivedFrom":subQ1}),-1.0]])]});}
            extrude(context, id + "F1", {"entities" : qUnion([Q0, Q1, Q2, Q3, Q4, Q5, Q6, Q7, Q8, Q9, Q10, Q11, Q12, Q13, Q14, Q15, Q16, Q17, Q18, Q19, Q20, Q21, Q22, Q23, Q24, Q25, Q26, Q27, Q28, Q29, Q30, Q31, Q32, Q33, Q34, Q35, Q36, Q37, Q38, Q39, Q40, Q41, Q42, Q43, Q44, Q45, Q46, Q47, Q48, Q49, Q50, Q51, Q52, Q53, Q54, Q55, Q56, Q57, Q58, Q59, Q60, Q61, Q62, Q63, Q64, Q65, Q66, Q67, Q68, Q69, Q70, Q71, Q72, Q73, Q74, Q75, Q76, Q77, Q78, Q79, Q80, Q81, Q82, Q83]), "depth" : 7 * mm, "offsetDistance" : 25.4 * mm});
        }
        {
            var Q0;
            {var subQ0=sQuery(id+"F0.wireOp",EDGE,"E28");Q0=makeQuery(id+"F1.opExtrude","CAP_EDGE",EDGE,{"disambiguationData":[OSD([subQ0]),TDD([makeQuery(id+"F0.imprint","IMPRINT",EDGE,{"disambiguationData":[TD([[makeQuery(id+"F0.imprint","INTERSECT",VERTEX,{"derivedFrom":[sQuery(id+"F0.wireOp",EDGE,"E21"),subQ0]}),1.0]])],"derivedFrom":subQ0})])],"isStart":true});}
            var Q1;
            Q1=makeQuery(id+"F1.opExtrude","CAP_EDGE",EDGE,{"disambiguationData":[OSD([sQuery(id+"F0.wireOp",EDGE,"E21")])],"isStart":true});
            var Q2;
            {var subQ0=sQuery(id+"F0.wireOp",EDGE,"E27");Q2=makeQuery(id+"F1.opExtrude","CAP_EDGE",EDGE,{"disambiguationData":[OSD([subQ0]),TDD([makeQuery(id+"F0.imprint","IMPRINT",EDGE,{"disambiguationData":[TD([[makeQuery(id+"F0.imprint","INTERSECT",VERTEX,{"derivedFrom":[sQuery(id+"F0.wireOp",EDGE,"E21"),subQ0]}),-1.0]])],"derivedFrom":subQ0})])],"isStart":true});}
            var Q3;
            Q3=makeQuery(id+"F1.opExtrude","CAP_EDGE",EDGE,{"disambiguationData":[OSD([sQuery(id+"F0.wireOp",EDGE,"E22")])],"isStart":true});
            var Q4;
            {var subQ0=sQuery(id+"F0.wireOp",EDGE,"E32");Q4=makeQuery(id+"F1.opExtrude","CAP_EDGE",EDGE,{"disambiguationData":[OSD([subQ0]),TDD([makeQuery(id+"F0.imprint","IMPRINT",EDGE,{"disambiguationData":[TD([[makeQuery(id+"F0.imprint","INTERSECT",VERTEX,{"derivedFrom":[sQuery(id+"F0.wireOp",EDGE,"E22"),subQ0]}),-1.0]])],"derivedFrom":subQ0})])],"isStart":true});}
            var Q5;
            Q5=makeQuery(id+"F1.opExtrude","CAP_EDGE",EDGE,{"disambiguationData":[OSD([sQuery(id+"F0.wireOp",EDGE,"E25")])],"isStart":true});
            var Q6;
            {var subQ0=sQuery(id+"F0.wireOp",EDGE,"E31");Q6=makeQuery(id+"F1.opExtrude","CAP_EDGE",EDGE,{"disambiguationData":[OSD([subQ0]),TDD([makeQuery(id+"F0.imprint","IMPRINT",EDGE,{"disambiguationData":[TD([[makeQuery(id+"F0.imprint","INTERSECT",VERTEX,{"derivedFrom":[sQuery(id+"F0.wireOp",EDGE,"E24"),subQ0]}),1.0]])],"derivedFrom":subQ0})])],"isStart":true});}
            var Q7;
            Q7=makeQuery(id+"F1.opExtrude","CAP_EDGE",EDGE,{"disambiguationData":[OSD([sQuery(id+"F0.wireOp",EDGE,"E24")])],"isStart":true});
            var Q8;
            {var subQ0=sQuery(id+"F0.wireOp",EDGE,"E30");Q8=makeQuery(id+"F1.opExtrude","CAP_EDGE",EDGE,{"disambiguationData":[OSD([subQ0]),TDD([makeQuery(id+"F0.imprint","IMPRINT",EDGE,{"disambiguationData":[TD([[makeQuery(id+"F0.imprint","INTERSECT",VERTEX,{"derivedFrom":[sQuery(id+"F0.wireOp",EDGE,"E23"),subQ0]}),1.0]])],"derivedFrom":subQ0})])],"isStart":true});}
            var Q9;
            Q9=makeQuery(id+"F1.opExtrude","CAP_EDGE",EDGE,{"disambiguationData":[OSD([sQuery(id+"F0.wireOp",EDGE,"E23")])],"isStart":true});
            var Q10;
            {var subQ0=sQuery(id+"F0.wireOp",EDGE,"E29");Q10=makeQuery(id+"F1.opExtrude","CAP_EDGE",EDGE,{"disambiguationData":[OSD([subQ0]),TDD([makeQuery(id+"F0.imprint","IMPRINT",EDGE,{"disambiguationData":[TD([[makeQuery(id+"F0.imprint","INTERSECT",VERTEX,{"derivedFrom":[sQuery(id+"F0.wireOp",EDGE,"E23"),subQ0]}),-1.0]])],"derivedFrom":subQ0})])],"isStart":true});}
            var Q11;
            Q11=makeQuery(id+"F1.opExtrude","CAP_EDGE",EDGE,{"disambiguationData":[OSD([sQuery(id+"F0.wireOp",EDGE,"E26")])],"isStart":true});
            var Q12;
            {var subQ0=sQuery(id+"F0.wireOp",EDGE,"E28");Q12=makeQuery(id+"F1.opExtrude","CAP_EDGE",EDGE,{"disambiguationData":[OSD([subQ0]),TDD([makeQuery(id+"F0.imprint","IMPRINT",EDGE,{"disambiguationData":[TD([[makeQuery(id+"F0.imprint","INTERSECT",VERTEX,{"derivedFrom":[sQuery(id+"F0.wireOp",EDGE,"E21"),subQ0]}),1.0]])],"derivedFrom":subQ0})])],"isStart":false});}
            var Q13;
            Q13=makeQuery(id+"F1.opExtrude","CAP_EDGE",EDGE,{"disambiguationData":[OSD([sQuery(id+"F0.wireOp",EDGE,"E21")])],"isStart":false});
            var Q14;
            {var subQ0=sQuery(id+"F0.wireOp",EDGE,"E27");Q14=makeQuery(id+"F1.opExtrude","CAP_EDGE",EDGE,{"disambiguationData":[OSD([subQ0]),TDD([makeQuery(id+"F0.imprint","IMPRINT",EDGE,{"disambiguationData":[TD([[makeQuery(id+"F0.imprint","INTERSECT",VERTEX,{"derivedFrom":[sQuery(id+"F0.wireOp",EDGE,"E21"),subQ0]}),-1.0]])],"derivedFrom":subQ0})])],"isStart":false});}
            var Q15;
            Q15=makeQuery(id+"F1.opExtrude","CAP_EDGE",EDGE,{"disambiguationData":[OSD([sQuery(id+"F0.wireOp",EDGE,"E26")])],"isStart":false});
            var Q16;
            {var subQ0=sQuery(id+"F0.wireOp",EDGE,"E29");Q16=makeQuery(id+"F1.opExtrude","CAP_EDGE",EDGE,{"disambiguationData":[OSD([subQ0]),TDD([makeQuery(id+"F0.imprint","IMPRINT",EDGE,{"disambiguationData":[TD([[makeQuery(id+"F0.imprint","INTERSECT",VERTEX,{"derivedFrom":[sQuery(id+"F0.wireOp",EDGE,"E23"),subQ0]}),-1.0]])],"derivedFrom":subQ0})])],"isStart":false});}
            var Q17;
            Q17=makeQuery(id+"F1.opExtrude","CAP_EDGE",EDGE,{"disambiguationData":[OSD([sQuery(id+"F0.wireOp",EDGE,"E23")])],"isStart":false});
            var Q18;
            {var subQ0=sQuery(id+"F0.wireOp",EDGE,"E30");Q18=makeQuery(id+"F1.opExtrude","CAP_EDGE",EDGE,{"disambiguationData":[OSD([subQ0]),TDD([makeQuery(id+"F0.imprint","IMPRINT",EDGE,{"disambiguationData":[TD([[makeQuery(id+"F0.imprint","INTERSECT",VERTEX,{"derivedFrom":[sQuery(id+"F0.wireOp",EDGE,"E23"),subQ0]}),1.0]])],"derivedFrom":subQ0})])],"isStart":false});}
            var Q19;
            Q19=makeQuery(id+"F1.opExtrude","CAP_EDGE",EDGE,{"disambiguationData":[OSD([sQuery(id+"F0.wireOp",EDGE,"E24")])],"isStart":false});
            var Q20;
            {var subQ0=sQuery(id+"F0.wireOp",EDGE,"E31");Q20=makeQuery(id+"F1.opExtrude","CAP_EDGE",EDGE,{"disambiguationData":[OSD([subQ0]),TDD([makeQuery(id+"F0.imprint","IMPRINT",EDGE,{"disambiguationData":[TD([[makeQuery(id+"F0.imprint","INTERSECT",VERTEX,{"derivedFrom":[sQuery(id+"F0.wireOp",EDGE,"E24"),subQ0]}),1.0]])],"derivedFrom":subQ0})])],"isStart":false});}
            var Q21;
            Q21=makeQuery(id+"F1.opExtrude","CAP_EDGE",EDGE,{"disambiguationData":[OSD([sQuery(id+"F0.wireOp",EDGE,"E25")])],"isStart":false});
            var Q22;
            {var subQ0=sQuery(id+"F0.wireOp",EDGE,"E32");Q22=makeQuery(id+"F1.opExtrude","CAP_EDGE",EDGE,{"disambiguationData":[OSD([subQ0]),TDD([makeQuery(id+"F0.imprint","IMPRINT",EDGE,{"disambiguationData":[TD([[makeQuery(id+"F0.imprint","INTERSECT",VERTEX,{"derivedFrom":[sQuery(id+"F0.wireOp",EDGE,"E22"),subQ0]}),-1.0]])],"derivedFrom":subQ0})])],"isStart":false});}
            var Q23;
            Q23=makeQuery(id+"F1.opExtrude","CAP_EDGE",EDGE,{"disambiguationData":[OSD([sQuery(id+"F0.wireOp",EDGE,"E22")])],"isStart":false});
            fillet(context, id + "F2", {"entities" : qUnion([Q0, Q1, Q2, Q3, Q4, Q5, Q6, Q7, Q8, Q9, Q10, Q11, Q12, Q13, Q14, Q15, Q16, Q17, Q18, Q19, Q20, Q21, Q22, Q23]), "radius" : 3.28 * mm, "tangentPropagation" : true, "allowEdgeOverflow" : false});
        }
    });
